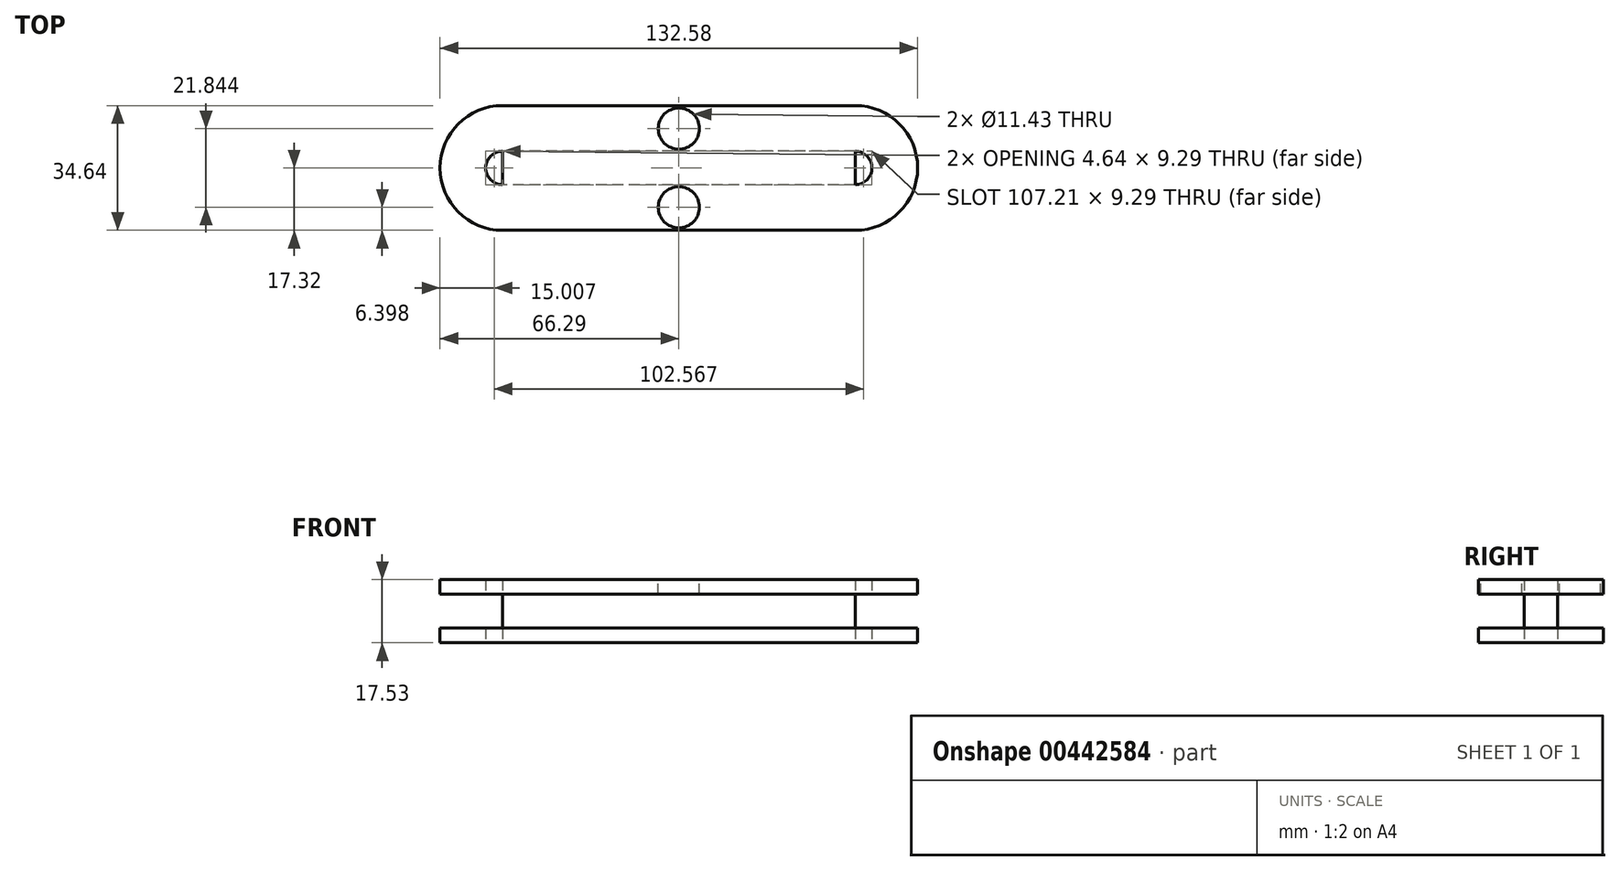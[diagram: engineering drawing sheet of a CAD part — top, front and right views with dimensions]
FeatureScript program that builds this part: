
annotation { "Feature Type Name" : "Feature", "Feature Type Description" : "" }
export const myFeature = defineFeature(function(context is Context, id is Id, definition is map)
    precondition{}
    {
        {
            var Q0;
            Q0=qCreatedBy(makeId("Top.planeOp"),FACE);
            var sketch = newSketch(context, id + "F0", { "sketchPlane" : qUnion([Q0])});
            skLineSegment(sketch, "E0.bottom", {"start": v(48.96, 17.32) * mm, "end": v(-48.96, 17.32) * mm});
            skLineSegment(sketch, "E0.top", {"start": v(48.96, -17.32) * mm, "end": v(-48.96, -17.32) * mm});
            skLineSegment(sketch, "E0.left", {"start": v(48.96, 17.32) * mm, "end": v(48.96, -17.32) * mm});
            skLineSegment(sketch, "E0.right", {"start": v(-48.96, 17.32) * mm, "end": v(-48.96, -17.32) * mm});
            skPoint(sketch, "E0.middle", {"position": v(0, 0) * mm});
            skArc(sketch, "E1", {"start": v(-48.96, 17.32) * mm, "mid": v(-66.29, 0) * mm, "end": v(-48.96, -17.32) * mm});
            skArc(sketch, "E2", {"start": v(48.96, -17.32) * mm, "mid": v(66.29, 0) * mm, "end": v(48.96, 17.32) * mm});
            skLineSegment(sketch, "E3.bottom", {"start": v(48.96, 4.64) * mm, "end": v(-48.96, 4.64) * mm});
            skLineSegment(sketch, "E3.top", {"start": v(48.96, -4.64) * mm, "end": v(-48.96, -4.64) * mm});
            skLineSegment(sketch, "E3.left", {"start": v(48.96, 4.64) * mm, "end": v(48.96, -4.64) * mm});
            skLineSegment(sketch, "E3.right", {"start": v(-48.96, 4.64) * mm, "end": v(-48.96, -4.64) * mm});
            skArc(sketch, "E4", {"start": v(-48.96, 4.64) * mm, "mid": v(-53.6, 0) * mm, "end": v(-48.96, -4.64) * mm});
            skArc(sketch, "E5", {"start": v(48.96, -4.64) * mm, "mid": v(53.6, 0) * mm, "end": v(48.96, 4.64) * mm});
            skSolve(sketch);
        }
        {
            var Q0;
            Q0=makeQuery(id+"F0.imprint","IMPRINT",FACE,{"disambiguationData":[TD([[makeQuery(id+"F0.imprint","IMPRINT",EDGE,{"derivedFrom":sQuery(id+"F0.wireOp",EDGE,"E3.bottom")}),1.0]])]});
            var Q1;
            Q1=makeQuery(id+"F0.imprint","IMPRINT",FACE,{"disambiguationData":[TD([[makeQuery(id+"F0.imprint","IMPRINT",EDGE,{"derivedFrom":sQuery(id+"F0.wireOp",EDGE,"E3.left")}),1.0]])]});
            var Q2;
            Q2=makeQuery(id+"F0.imprint","IMPRINT",FACE,{"disambiguationData":[TD([[makeQuery(id+"F0.imprint","IMPRINT",EDGE,{"derivedFrom":sQuery(id+"F0.wireOp",EDGE,"E3.right")}),-1.0]])]});
            extrude(context, id + "F1", {"entities" : qUnion([Q0, Q1, Q2]), "depth" : 13.72 * mm, "offsetDistance" : 25.4 * mm, "hasSecondDirection" : true, "secondDirectionOppositeDirection" : true, "secondDirectionDepth" : 3.8 * mm});
        }
        {
            var Q0;
            {var subQ0=sQuery(id+"F0.wireOp",EDGE,"E0.top");Q0=makeQuery(id+"F0.imprint","IMPRINT",FACE,{"disambiguationData":[TD([[makeQuery(id+"F0.imprint","IMPRINT",EDGE,{"derivedFrom":subQ0}),-1.0]])]});}
            var Q1;
            {var subQ0=sQuery(id+"F0.wireOp",EDGE,"E1");Q1=makeQuery(id+"F0.imprint","IMPRINT",FACE,{"disambiguationData":[TD([[makeQuery(id+"F0.imprint","IMPRINT",EDGE,{"derivedFrom":subQ0}),1.0]])]});}
            var Q2;
            {var subQ0=sQuery(id+"F0.wireOp",EDGE,"E0.bottom");Q2=makeQuery(id+"F0.imprint","IMPRINT",FACE,{"disambiguationData":[TD([[makeQuery(id+"F0.imprint","IMPRINT",EDGE,{"derivedFrom":subQ0}),1.0]])]});}
            var Q3;
            {var subQ0=sQuery(id+"F0.wireOp",EDGE,"E2");Q3=makeQuery(id+"F0.imprint","IMPRINT",FACE,{"disambiguationData":[TD([[makeQuery(id+"F0.imprint","IMPRINT",EDGE,{"derivedFrom":subQ0}),1.0]])]});}
            extrude(context, id + "F2", {"entities" : qUnion([Q0, Q1, Q2, Q3]), "operationType" : NewBodyOperationType.ADD, "depth" : 0.25 * mm, "offsetDistance" : 25.4 * mm, "hasSecondDirection" : true, "secondDirectionOppositeDirection" : true, "secondDirectionDepth" : 3.8 * mm});
        }
        {
            var Q0;
            Q0=makeQuery(id+"F2.opExtrude","CAP_FACE",FACE,{"disambiguationData":[OSD([sQuery(id+"F0.wireOp",EDGE,"E0.bottom"),sQuery(id+"F0.wireOp",EDGE,"E0.top"),sQuery(id+"F0.wireOp",EDGE,"E1"),sQuery(id+"F0.wireOp",EDGE,"E2"),sQuery(id+"F0.wireOp",EDGE,"E3.bottom"),sQuery(id+"F0.wireOp",EDGE,"E3.top"),sQuery(id+"F0.wireOp",EDGE,"E4"),sQuery(id+"F0.wireOp",EDGE,"E5")])],"isStart":false});
            extrude(context, id + "F3", {"entities" : qUnion([Q0]), "operationType" : NewBodyOperationType.ADD, "depth" : 13.46 * mm, "offsetDistance" : 25.4 * mm, "hasSecondDirection" : true, "secondDirectionOppositeDirection" : false, "secondDirectionDepth" : 9.4 * mm});
        }
        {
            var Q0;
            {var subQ0=sQuery(id+"F0.wireOp",EDGE,"E5");var subQ1=sQuery(id+"F0.wireOp",EDGE,"E4");var subQ2=sQuery(id+"F0.wireOp",EDGE,"E3.top");var subQ3=sQuery(id+"F0.wireOp",EDGE,"E3.bottom");Q0=makeQuery(id+"F3.boolean.opBoolean","MERGE",FACE,{"derivedFrom":[makeQuery(id+"F1.opExtrude","CAP_FACE",FACE,{"disambiguationData":[OSD([subQ3,subQ2,subQ1,subQ0])],"isStart":false}),makeQuery(id+"F3.opExtrude","CAP_FACE",FACE,{"disambiguationData":[OSD([sQuery(id+"F0.wireOp",EDGE,"E0.bottom"),sQuery(id+"F0.wireOp",EDGE,"E0.top"),sQuery(id+"F0.wireOp",EDGE,"E1"),sQuery(id+"F0.wireOp",EDGE,"E2"),subQ3,subQ2,subQ1,subQ0])],"isStart":false})]});}
            var sketch = newSketch(context, id + "F4", { "sketchPlane" : qUnion([Q0])});
            skCircle(sketch, "E6", {"center": v(0, 10.92) * mm, "radius": 5.72 * mm});
            skCircle(sketch, "E7", {"center": v(0, -10.92) * mm, "radius": 5.72 * mm});
            skSolve(sketch);
        }
        {
            var Q0;
            Q0 = qSketchRegion(id + "F4", true);
            extrude(context, id + "F5", {"entities" : qUnion([Q0]), "operationType" : NewBodyOperationType.REMOVE, "oppositeDirection" : true, "depth" : 4.57 * mm, "offsetDistance" : 25.4 * mm});
        }
    });
